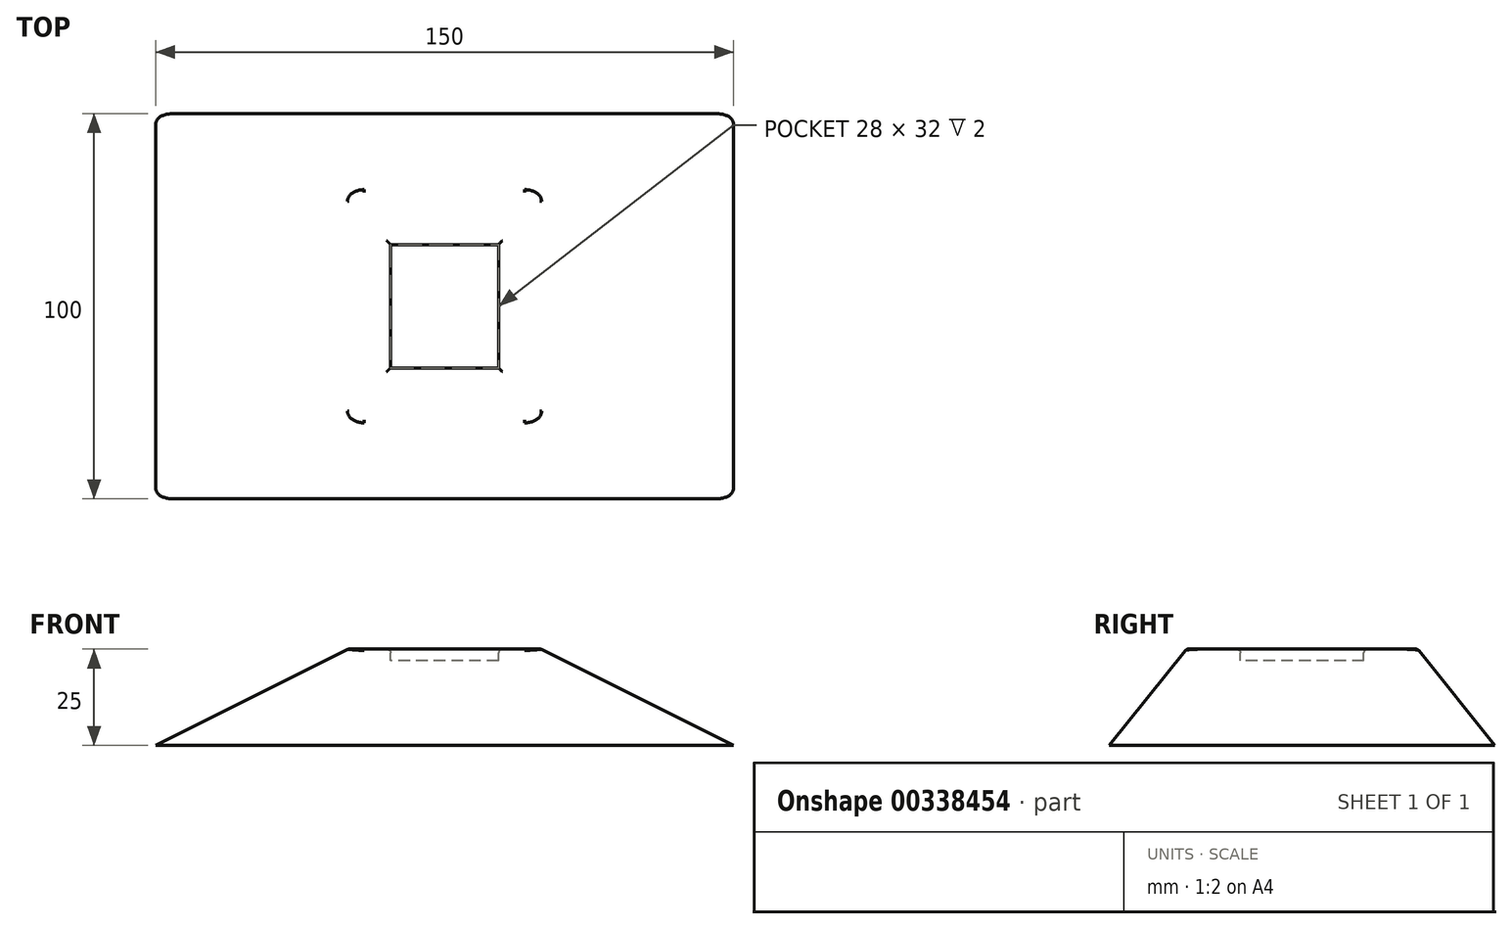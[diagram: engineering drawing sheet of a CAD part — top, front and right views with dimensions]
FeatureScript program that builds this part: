
annotation { "Feature Type Name" : "Feature", "Feature Type Description" : "" }
export const myFeature = defineFeature(function(context is Context, id is Id, definition is map)
    precondition{}
    {
        {
            var Q0;
            Q0=qCreatedBy(makeId("Top.planeOp"),FACE);
            var sketch = newSketch(context, id + "F0", { "sketchPlane" : qUnion([Q0])});
            skLineSegment(sketch, "E0.bottom", {"start": v(75, -50) * mm, "end": v(-75, -50) * mm});
            skLineSegment(sketch, "E0.top", {"start": v(75, 50) * mm, "end": v(-75, 50) * mm});
            skLineSegment(sketch, "E0.left", {"start": v(75, -50) * mm, "end": v(75, 50) * mm});
            skLineSegment(sketch, "E0.right", {"start": v(-75, -50) * mm, "end": v(-75, 50) * mm});
            skPoint(sketch, "E0.middle", {"position": v(0, 0) * mm});
            skSolve(sketch);
        }
        {
            var Q0;
            Q0=qSketchRegion(id+"F0",true);
            extrude(context, id + "F1", {"entities" : qUnion([Q0]), "depth" : 25 * mm});
        }
        {
            var Q0;
            Q0=makeQuery(id+"F1.opExtrude","SWEPT_FACE",FACE,{"disambiguationData":[OSD([sQuery(id+"F0.wireOp",EDGE,"E0.bottom")])]});
            var sketch = newSketch(context, id + "F2", { "sketchPlane" : qUnion([Q0])});
            skLineSegment(sketch, "E1", {"start": v(-75, 0) * mm, "end": v(75, 0) * mm});
            skLineSegment(sketch, "E2", {"start": v(0, 25) * mm, "end": v(-25, 25) * mm});
            skLineSegment(sketch, "E3.MirrorCS", {"start": v(0, 25) * mm, "end": v(25, 25) * mm});
            skLineSegment(sketch, "E4", {"start": v(-75, 0) * mm, "end": v(-25, 25) * mm});
            skLineSegment(sketch, "E5", {"start": v(25, 25) * mm, "end": v(75, 0) * mm});
            skSolve(sketch);
        }
        {
            var Q0;
            Q0=qSketchRegion(id+"F2",true);
            var Q1;
            Q1=makeQuery(id+"F1.opExtrude","SWEPT_FACE",FACE,{"disambiguationData":[OSD([sQuery(id+"F0.wireOp",EDGE,"E0.top")])]});
            extrude(context, id + "F3", {"entities" : qUnion([Q0]), "endBound" : BoundingType.UP_TO_SURFACE, "oppositeDirection" : true, "endBoundEntityFace" : qUnion([Q1]), "depth" : 25 * mm});
        }
        {
            var Q0;
            Q0=makeQuery(id+"F1.opExtrude","SWEPT_FACE",FACE,{"disambiguationData":[OSD([sQuery(id+"F0.wireOp",EDGE,"E0.left")])]});
            var sketch = newSketch(context, id + "F4", { "sketchPlane" : qUnion([Q0])});
            skLineSegment(sketch, "E6", {"start": v(-50, 0) * mm, "end": v(50, 0) * mm});
            skLineSegment(sketch, "E7", {"start": v(0, 25) * mm, "end": v(-30, 25) * mm});
            skLineSegment(sketch, "E8.MirrorCS", {"start": v(0, 25) * mm, "end": v(30, 25) * mm});
            skLineSegment(sketch, "E9", {"start": v(-50, 0) * mm, "end": v(-30, 25) * mm});
            skLineSegment(sketch, "E10", {"start": v(30, 25) * mm, "end": v(50, 0) * mm});
            skSolve(sketch);
        }
        {
            var Q0;
            Q0=makeQuery(id+"F4.imprint","IMPRINT",FACE,{"disambiguationData":[TD([[makeQuery(id+"F4.imprint","IMPRINT",EDGE,{"derivedFrom":sQuery(id+"F4.wireOp",EDGE,"E6")}),1.0]])]});
            var Q1;
            Q1=makeQuery(id+"F1.opExtrude","SWEPT_FACE",FACE,{"disambiguationData":[OSD([sQuery(id+"F0.wireOp",EDGE,"E0.right")])]});
            extrude(context, id + "F5", {"entities" : qUnion([Q0]), "endBound" : BoundingType.UP_TO_SURFACE, "oppositeDirection" : true, "endBoundEntityFace" : qUnion([Q1]), "depth" : 25 * mm});
        }
        {
            var Q0;
            Q0=makeQuery(id+"F1.opExtrude","SWEPT_BODY",BODY,{"disambiguationData":[OSD([sQuery(id+"F0.wireOp",EDGE,"E0.bottom"),sQuery(id+"F0.wireOp",EDGE,"E0.top"),sQuery(id+"F0.wireOp",EDGE,"E0.left"),sQuery(id+"F0.wireOp",EDGE,"E0.right")])]});
            var Q1;
            Q1=makeQuery(id+"F3.opExtrude","SWEPT_BODY",BODY,{"disambiguationData":[OSD([sQuery(id+"F2.wireOp",EDGE,"E1"),sQuery(id+"F2.wireOp",EDGE,"E2"),sQuery(id+"F2.wireOp",EDGE,"E3.MirrorCS"),sQuery(id+"F2.wireOp",EDGE,"E4"),sQuery(id+"F2.wireOp",EDGE,"E5")])]});
            var Q2;
            Q2=makeQuery(id+"F5.opExtrude","SWEPT_BODY",BODY,{"disambiguationData":[OSD([sQuery(id+"F4.wireOp",EDGE,"E6"),sQuery(id+"F4.wireOp",EDGE,"E7"),sQuery(id+"F4.wireOp",EDGE,"E8.MirrorCS"),sQuery(id+"F4.wireOp",EDGE,"E9"),sQuery(id+"F4.wireOp",EDGE,"E10")])]});
            booleanBodies(context, id + "F6", {"operationType" : BooleanOperationType.INTERSECTION, "tools" : qUnion([Q0, Q1, Q2])});
        }
        {
            var Q0;
            Q0=makeQuery(id+"F6.opBoolean","INTERSECT",EDGE,{"derivedFrom":[makeQuery(id+"F3.opExtrude","SWEPT_FACE",FACE,{"disambiguationData":[OSD([sQuery(id+"F2.wireOp",EDGE,"E4")])]}),makeQuery(id+"F5.opExtrude","SWEPT_FACE",FACE,{"disambiguationData":[OSD([sQuery(id+"F4.wireOp",EDGE,"E10")])]})]});
            var Q1;
            Q1=makeQuery(id+"F6.opBoolean","INTERSECT",EDGE,{"derivedFrom":[makeQuery(id+"F3.opExtrude","SWEPT_FACE",FACE,{"disambiguationData":[OSD([sQuery(id+"F2.wireOp",EDGE,"E4")])]}),makeQuery(id+"F5.opExtrude","SWEPT_FACE",FACE,{"disambiguationData":[OSD([sQuery(id+"F4.wireOp",EDGE,"E9")])]})]});
            var Q2;
            Q2=makeQuery(id+"F6.opBoolean","INTERSECT",EDGE,{"derivedFrom":[makeQuery(id+"F3.opExtrude","SWEPT_FACE",FACE,{"disambiguationData":[OSD([sQuery(id+"F2.wireOp",EDGE,"E5")])]}),makeQuery(id+"F5.opExtrude","SWEPT_FACE",FACE,{"disambiguationData":[OSD([sQuery(id+"F4.wireOp",EDGE,"E9")])]})]});
            var Q3;
            Q3=makeQuery(id+"F6.opBoolean","INTERSECT",EDGE,{"derivedFrom":[makeQuery(id+"F3.opExtrude","SWEPT_FACE",FACE,{"disambiguationData":[OSD([sQuery(id+"F2.wireOp",EDGE,"E5")])]}),makeQuery(id+"F5.opExtrude","SWEPT_FACE",FACE,{"disambiguationData":[OSD([sQuery(id+"F4.wireOp",EDGE,"E10")])]})]});
            var Q4;
            Q4=makeQuery(id+"F5.opExtrude","SWEPT_EDGE",EDGE,{"disambiguationData":[OSD([sQuery(id+"F0.wireOp",EDGE,"E0.left"),sQuery(id+"F4.wireOp",EDGE,"E7"),sQuery(id+"F4.wireOp",EDGE,"E9")])]});
            var Q5;
            Q5=makeQuery(id+"F3.opExtrude","SWEPT_EDGE",EDGE,{"disambiguationData":[OSD([sQuery(id+"F0.wireOp",EDGE,"E0.bottom"),sQuery(id+"F2.wireOp",EDGE,"E2"),sQuery(id+"F2.wireOp",EDGE,"E4")])]});
            var Q6;
            Q6=makeQuery(id+"F5.opExtrude","SWEPT_EDGE",EDGE,{"disambiguationData":[OSD([sQuery(id+"F0.wireOp",EDGE,"E0.left"),sQuery(id+"F4.wireOp",EDGE,"E8.MirrorCS"),sQuery(id+"F4.wireOp",EDGE,"E10")])]});
            var Q7;
            Q7=makeQuery(id+"F3.opExtrude","SWEPT_EDGE",EDGE,{"disambiguationData":[OSD([sQuery(id+"F0.wireOp",EDGE,"E0.bottom"),sQuery(id+"F2.wireOp",EDGE,"E3.MirrorCS"),sQuery(id+"F2.wireOp",EDGE,"E5")])]});
            fillet(context, id + "F7", {"entities" : qUnion([Q0, Q1, Q2, Q3, Q4, Q5, Q6, Q7]), "radius" : 5 * mm, "tangentPropagation" : true, "allowEdgeOverflow" : false});
        }
        {
            var Q0;
            Q0=makeQuery(id+"F1.opExtrude","CAP_FACE",FACE,{"disambiguationData":[OSD([sQuery(id+"F0.wireOp",EDGE,"E0.bottom"),sQuery(id+"F0.wireOp",EDGE,"E0.top"),sQuery(id+"F0.wireOp",EDGE,"E0.left"),sQuery(id+"F0.wireOp",EDGE,"E0.right")])],"isStart":false});
            var sketch = newSketch(context, id + "F8", { "sketchPlane" : qUnion([Q0])});
            skLineSegment(sketch, "E11.bottom", {"start": v(14, 16) * mm, "end": v(-14, 16) * mm});
            skLineSegment(sketch, "E11.top", {"start": v(14, -16) * mm, "end": v(-14, -16) * mm});
            skLineSegment(sketch, "E11.left", {"start": v(14, 16) * mm, "end": v(14, -16) * mm});
            skLineSegment(sketch, "E11.right", {"start": v(-14, 16) * mm, "end": v(-14, -16) * mm});
            skPoint(sketch, "E11.middle", {"position": v(0, 0) * mm});
            skSolve(sketch);
        }
        {
            var Q0;
            Q0=makeQuery(id+"F8.imprint","IMPRINT",FACE,{"disambiguationData":[TD([[makeQuery(id+"F8.imprint","IMPRINT",EDGE,{"derivedFrom":sQuery(id+"F8.wireOp",EDGE,"E11.bottom")}),1.0]])]});
            extrude(context, id + "F9", {"entities" : qUnion([Q0]), "operationType" : NewBodyOperationType.REMOVE, "oppositeDirection" : true, "depth" : 3 * mm});
        }
        {
            var Q0;
            Q0=makeQuery(id+"F9.boolean.opBoolean","COPY",EDGE,{"derivedFrom":makeQuery(id+"F9.opExtrude","CAP_EDGE",EDGE,{"disambiguationData":[OSD([sQuery(id+"F8.wireOp",EDGE,"E11.right")])],"isStart":true})});
            var Q1;
            Q1=makeQuery(id+"F9.boolean.opBoolean","COPY",EDGE,{"derivedFrom":makeQuery(id+"F9.opExtrude","CAP_EDGE",EDGE,{"disambiguationData":[OSD([sQuery(id+"F8.wireOp",EDGE,"E11.bottom")])],"isStart":true})});
            var Q2;
            Q2=makeQuery(id+"F1.opExtrude","CAP_FACE",FACE,{"disambiguationData":[OSD([sQuery(id+"F0.wireOp",EDGE,"E0.bottom"),sQuery(id+"F0.wireOp",EDGE,"E0.top"),sQuery(id+"F0.wireOp",EDGE,"E0.left"),sQuery(id+"F0.wireOp",EDGE,"E0.right")])],"isStart":false});
            fillet(context, id + "F10", {"entities" : qUnion([Q0, Q1, Q2]), "radius" : 1 * mm, "tangentPropagation" : true, "allowEdgeOverflow" : false});
        }
    });
